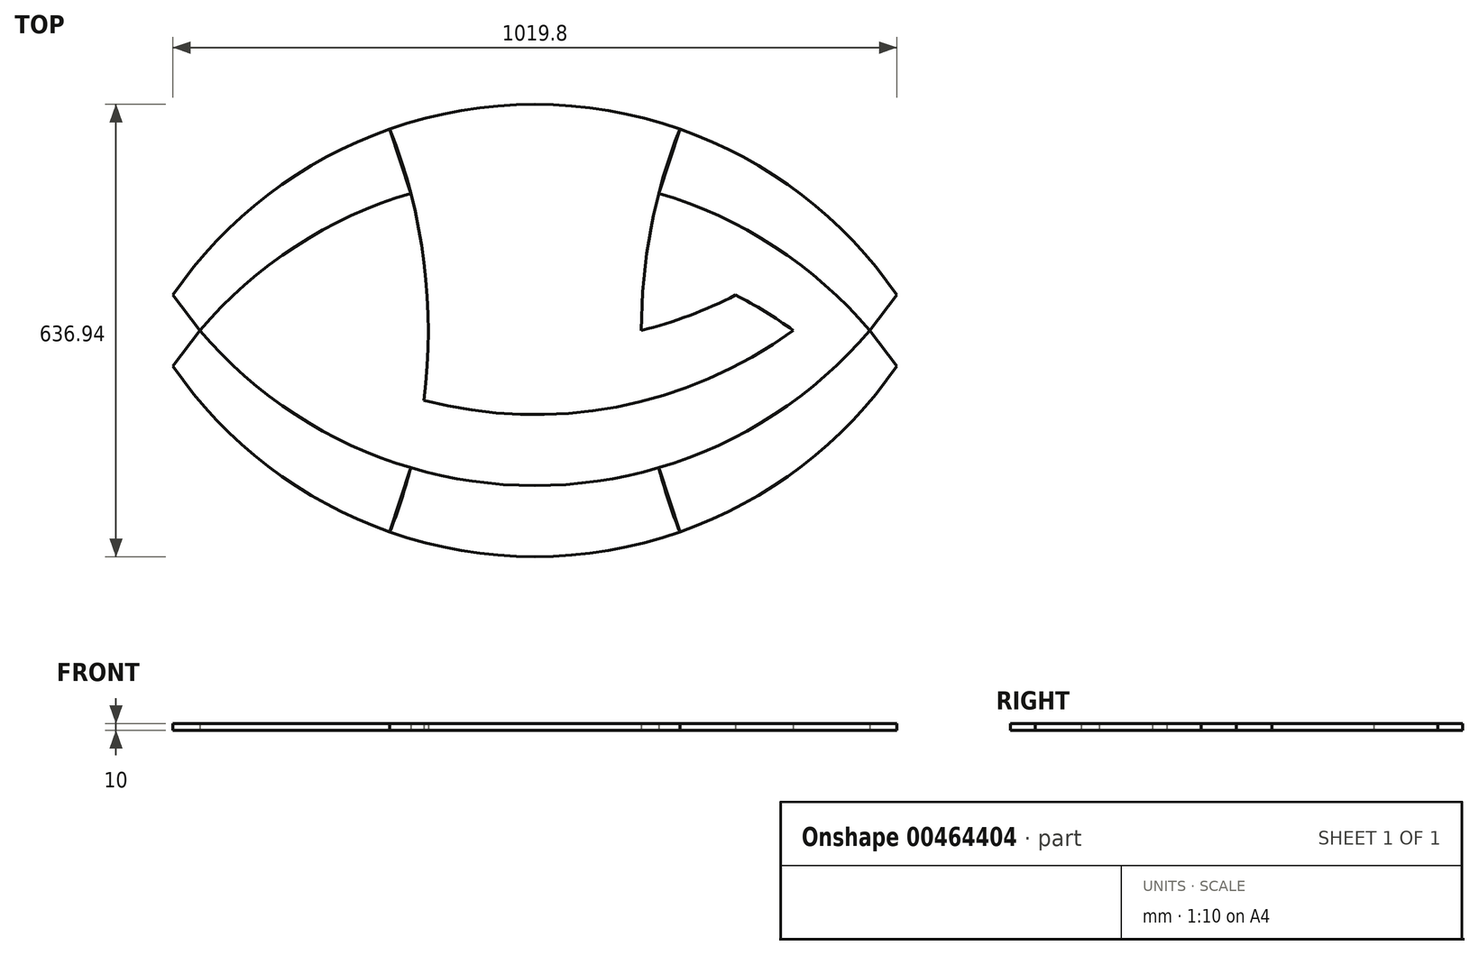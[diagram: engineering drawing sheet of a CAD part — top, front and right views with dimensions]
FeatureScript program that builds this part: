
annotation { "Feature Type Name" : "Feature", "Feature Type Description" : "" }
export const myFeature = defineFeature(function(context is Context, id is Id, definition is map)
    precondition{}
    {
        {
            var Q0;
            Q0=qCreatedBy(makeId("Top.planeOp"),FACE);
            var sketch = newSketch(context, id + "F0", { "sketchPlane" : qUnion([Q0])});
            skLineSegment(sketch, "E0", {"start": v(0, 652.5) * mm, "end": v(0, -479.98) * mm, "construction": true});
            skLineSegment(sketch, "E1", {"start": v(-841.35, 0) * mm, "end": v(906.92, 0) * mm, "construction": true});
            skLineSegment(sketch, "E2.bottom", {"start": v(150, 300) * mm, "end": v(-150, 300) * mm, "construction": true});
            skLineSegment(sketch, "E2.top", {"start": v(150, -300) * mm, "end": v(-150, -300) * mm, "construction": true});
            skLineSegment(sketch, "E2.left", {"start": v(150, 300) * mm, "end": v(150, -300) * mm, "construction": true});
            skLineSegment(sketch, "E2.right", {"start": v(-150, 300) * mm, "end": v(-150, -300) * mm, "construction": true});
            skPoint(sketch, "E2.middle", {"position": v(0, 0) * mm});
            skCircle(sketch, "E3", {"center": v(0, 0) * mm, "radius": 300 * mm, "construction": true});
            skCircle(sketch, "E4", {"center": v(0, -300) * mm, "radius": 618.47 * mm});
            skCircle(sketch, "E5", {"center": v(0, 0) * mm, "radius": 918.47 * mm, "construction": true});
            skCircle(sketch, "E6", {"center": v(918.47, 0) * mm, "radius": 768.47 * mm});
            skCircle(sketch, "E7", {"center": v(-918.47, 0) * mm, "radius": 768.47 * mm});
            skLineSegment(sketch, "E8", {"start": v(-839.1, -50) * mm, "end": v(1037.37, -50) * mm, "construction": true});
            skLineSegment(sketch, "E9.MirrorCS", {"start": v(-839.1, 50) * mm, "end": v(1037.37, 50) * mm, "construction": true});
            skCircle(sketch, "E10.MirrorC", {"center": v(0, 400) * mm, "radius": 618.47 * mm});
            skCircle(sketch, "E11.MirrorC", {"center": v(0, -200) * mm, "radius": 618.47 * mm});
            skCircle(sketch, "E12.MirrorC", {"center": v(0, -400) * mm, "radius": 618.47 * mm});
            skCircle(sketch, "E13.MirrorC", {"center": v(0, -500) * mm, "radius": 618.47 * mm});
            skCircle(sketch, "E14.MirrorC", {"center": v(0, 100) * mm, "radius": 618.47 * mm});
            skCircle(sketch, "E15.MirrorC", {"center": v(0, 200) * mm, "radius": 618.47 * mm});
            skCircle(sketch, "E16.MirrorC", {"center": v(0, 600) * mm, "radius": 618.47 * mm});
            skCircle(sketch, "E17.MirrorC", {"center": v(0, 500) * mm, "radius": 618.47 * mm});
            skCircle(sketch, "E18.MirrorC", {"center": v(0, 300) * mm, "radius": 618.47 * mm});
            skLineSegment(sketch, "E19", {"start": v(-509.9, 50) * mm, "end": v(-471.7, 0) * mm});
            skLineSegment(sketch, "E20", {"start": v(-471.7, 0) * mm, "end": v(-509.9, -50) * mm});
            skLineSegment(sketch, "E21", {"start": v(509.9, 50) * mm, "end": v(471.7, 0) * mm});
            skLineSegment(sketch, "E22", {"start": v(471.7, 0) * mm, "end": v(509.9, -50) * mm});
            skLineSegment(sketch, "E23", {"start": v(204.3, 283.75) * mm, "end": v(174.7, 193.28) * mm});
            skLineSegment(sketch, "E24", {"start": v(204.3, -283.75) * mm, "end": v(174.7, -193.28) * mm});
            skLineSegment(sketch, "E25", {"start": v(-204.3, -283.75) * mm, "end": v(-174.7, -193.28) * mm});
            skLineSegment(sketch, "E26", {"start": v(-204.3, 283.75) * mm, "end": v(-174.7, 193.28) * mm});
            skSolve(sketch);
        }
        {
            var Q0;
            {var subQ0=sQuery(id+"F0.wireOp",EDGE,"E17.MirrorC");var subQ1=sQuery(id+"F0.wireOp",EDGE,"E4");var subQ2=makeQuery(id+"F0.imprint","INTERSECT",VERTEX,{"disambiguationData":[OD(1.0)],"derivedFrom":[subQ1,subQ0]});Q0=makeQuery(id+"F0.imprint","IMPRINT",FACE,{"disambiguationData":[TD([[makeQuery(id+"F0.imprint","IMPRINT",EDGE,{"disambiguationData":[TD([[subQ2,-1.0]])],"derivedFrom":subQ1}),1.0]])]});}
            var Q1;
            {var subQ0=sQuery(id+"F0.wireOp",EDGE,"E16.MirrorC");var subQ1=sQuery(id+"F0.wireOp",EDGE,"E4");var subQ2=makeQuery(id+"F0.imprint","INTERSECT",VERTEX,{"disambiguationData":[OD(1.0)],"derivedFrom":[subQ1,subQ0]});Q1=makeQuery(id+"F0.imprint","IMPRINT",FACE,{"disambiguationData":[TD([[makeQuery(id+"F0.imprint","IMPRINT",EDGE,{"disambiguationData":[TD([[subQ2,-1.0]])],"derivedFrom":subQ1}),1.0]])]});}
            var Q2;
            {var subQ0=sQuery(id+"F0.wireOp",EDGE,"7089ef92-c8cd-43ee-9cd9-a57d0f0e25173.MirrorC");var subQ1=sQuery(id+"F0.wireOp",EDGE,"E12.MirrorC");var subQ2=makeQuery(id+"F0.imprint","INTERSECT",VERTEX,{"disambiguationData":[OD(1.0)],"derivedFrom":[subQ1,subQ0]});Q2=makeQuery(id+"F0.imprint","IMPRINT",FACE,{"disambiguationData":[TD([[makeQuery(id+"F0.imprint","IMPRINT",EDGE,{"disambiguationData":[TD([[subQ2,-1.0]])],"derivedFrom":subQ1}),1.0]])]});}
            var Q3;
            {var subQ0=sQuery(id+"F0.wireOp",EDGE,"7089ef92-c8cd-43ee-9cd9-a57d0f0e25173.MirrorC");var subQ1=sQuery(id+"F0.wireOp",EDGE,"E6");var subQ2=makeQuery(id+"F0.imprint","INTERSECT",VERTEX,{"disambiguationData":[OD(1.0)],"derivedFrom":[subQ1,subQ0]});Q3=makeQuery(id+"F0.imprint","IMPRINT",FACE,{"disambiguationData":[TD([[makeQuery(id+"F0.imprint","IMPRINT",EDGE,{"disambiguationData":[TD([[subQ2,-1.0]])],"derivedFrom":subQ1}),1.0]])]});}
            var Q4;
            {var subQ0=sQuery(id+"F0.wireOp",EDGE,"7089ef92-c8cd-43ee-9cd9-a57d0f0e25173.MirrorC");var subQ1=sQuery(id+"F0.wireOp",EDGE,"E4");var subQ2=makeQuery(id+"F0.imprint","INTERSECT",VERTEX,{"disambiguationData":[OD(0.0)],"derivedFrom":[subQ1,subQ0]});Q4=makeQuery(id+"F0.imprint","IMPRINT",FACE,{"disambiguationData":[TD([[makeQuery(id+"F0.imprint","IMPRINT",EDGE,{"disambiguationData":[TD([[subQ2,-1.0]])],"derivedFrom":subQ1}),1.0]])]});}
            var Q5;
            {var subQ0=sQuery(id+"F0.wireOp",EDGE,"E17.MirrorC");var subQ1=sQuery(id+"F0.wireOp",EDGE,"E4");var subQ2=makeQuery(id+"F0.imprint","INTERSECT",VERTEX,{"disambiguationData":[OD(0.0)],"derivedFrom":[subQ1,subQ0]});Q5=makeQuery(id+"F0.imprint","IMPRINT",FACE,{"disambiguationData":[TD([[makeQuery(id+"F0.imprint","IMPRINT",EDGE,{"disambiguationData":[TD([[subQ2,-1.0]])],"derivedFrom":subQ1}),1.0]])]});}
            var Q6;
            {var subQ0=sQuery(id+"F0.wireOp",EDGE,"E20");Q6=makeQuery(id+"F0.imprint","IMPRINT",FACE,{"disambiguationData":[TD([[makeQuery(id+"F0.imprint","IMPRINT",EDGE,{"derivedFrom":subQ0}),1.0]])]});}
            var Q7;
            {var subQ0=sQuery(id+"F0.wireOp",EDGE,"E22");Q7=makeQuery(id+"F0.imprint","IMPRINT",FACE,{"disambiguationData":[TD([[makeQuery(id+"F0.imprint","IMPRINT",EDGE,{"derivedFrom":subQ0}),-1.0]])]});}
            var Q8;
            {var subQ0=sQuery(id+"F0.wireOp",EDGE,"E21");Q8=makeQuery(id+"F0.imprint","IMPRINT",FACE,{"disambiguationData":[TD([[makeQuery(id+"F0.imprint","IMPRINT",EDGE,{"derivedFrom":subQ0}),-1.0]])]});}
            var Q9;
            {var subQ0=sQuery(id+"F0.wireOp",EDGE,"E26");Q9=makeQuery(id+"F0.imprint","IMPRINT",FACE,{"disambiguationData":[TD([[makeQuery(id+"F0.imprint","IMPRINT",EDGE,{"derivedFrom":subQ0}),-1.0]])]});}
            var Q10;
            {var subQ0=sQuery(id+"F0.wireOp",EDGE,"E25");Q10=makeQuery(id+"F0.imprint","IMPRINT",FACE,{"disambiguationData":[TD([[makeQuery(id+"F0.imprint","IMPRINT",EDGE,{"derivedFrom":subQ0}),1.0]])]});}
            var Q11;
            {var subQ0=sQuery(id+"F0.wireOp",EDGE,"E24");Q11=makeQuery(id+"F0.imprint","IMPRINT",FACE,{"disambiguationData":[TD([[makeQuery(id+"F0.imprint","IMPRINT",EDGE,{"derivedFrom":subQ0}),-1.0]])]});}
            var Q12;
            {var subQ0=sQuery(id+"F0.wireOp",EDGE,"E23");Q12=makeQuery(id+"F0.imprint","IMPRINT",FACE,{"disambiguationData":[TD([[makeQuery(id+"F0.imprint","IMPRINT",EDGE,{"derivedFrom":subQ0}),1.0]])]});}
            extrude(context, id + "F1", {"entities" : qUnion([Q0, Q1, Q2, Q3, Q4, Q5, Q6, Q7, Q8, Q9, Q10, Q11, Q12]), "depth" : 10 * mm});
        }
        {
            var Q0;
            {var subQ0=sQuery(id+"F0.wireOp",EDGE,"E23");var subQ1=sQuery(id+"F0.wireOp",EDGE,"E6");var subQ2=sQuery(id+"F0.wireOp",EDGE,"E4");var subQ3=makeQuery(id+"F0.imprint","INTERSECT",VERTEX,{"derivedFrom":[subQ2,subQ1,subQ0]});Q0=makeQuery(id+"F0.imprint","IMPRINT",FACE,{"disambiguationData":[TD([[makeQuery(id+"F0.imprint","IMPRINT",EDGE,{"disambiguationData":[TD([[subQ3,-1.0]])],"derivedFrom":subQ2}),1.0]])]});}
            var Q1;
            {var subQ1=sQuery(id+"F0.wireOp",EDGE,"E6");var subQ3=sQuery(id+"F0.wireOp",EDGE,"E13.MirrorC");var subQ4=makeQuery(id+"F0.imprint","INTERSECT",VERTEX,{"disambiguationData":[OD(1.0)],"derivedFrom":[subQ1,subQ3]});Q1=makeQuery(id+"F0.imprint","IMPRINT",FACE,{"disambiguationData":[TD([[makeQuery(id+"F0.imprint","IMPRINT",EDGE,{"disambiguationData":[TD([[subQ4,-1.0]])],"derivedFrom":subQ3}),-1.0]])]});}
            var Q2;
            {var subQ0=sQuery(id+"F0.wireOp",EDGE,"E13.MirrorC");var subQ1=sQuery(id+"F0.wireOp",EDGE,"E6");var subQ2=makeQuery(id+"F0.imprint","INTERSECT",VERTEX,{"disambiguationData":[OD(1.0)],"derivedFrom":[subQ1,subQ0]});Q2=makeQuery(id+"F0.imprint","IMPRINT",FACE,{"disambiguationData":[TD([[makeQuery(id+"F0.imprint","IMPRINT",EDGE,{"disambiguationData":[TD([[subQ2,-1.0]])],"derivedFrom":subQ1}),-1.0]])]});}
            var Q3;
            {var subQ0=sQuery(id+"F0.wireOp",EDGE,"E16.MirrorC");var subQ1=sQuery(id+"F0.wireOp",EDGE,"E6");var subQ2=makeQuery(id+"F0.imprint","INTERSECT",VERTEX,{"disambiguationData":[OD(1.0)],"derivedFrom":[subQ1,subQ0]});Q3=makeQuery(id+"F0.imprint","IMPRINT",FACE,{"disambiguationData":[TD([[makeQuery(id+"F0.imprint","IMPRINT",EDGE,{"disambiguationData":[TD([[subQ2,-1.0]])],"derivedFrom":subQ1}),-1.0]])]});}
            var Q4;
            {var subQ1=sQuery(id+"F0.wireOp",EDGE,"E6");var subQ3=sQuery(id+"F0.wireOp",EDGE,"E17.MirrorC");var subQ4=makeQuery(id+"F0.imprint","INTERSECT",VERTEX,{"disambiguationData":[OD(1.0)],"derivedFrom":[subQ1,subQ3]});Q4=makeQuery(id+"F0.imprint","IMPRINT",FACE,{"disambiguationData":[TD([[makeQuery(id+"F0.imprint","IMPRINT",EDGE,{"disambiguationData":[TD([[subQ4,-1.0]])],"derivedFrom":subQ3}),1.0]])]});}
            var Q5;
            {var subQ0=sQuery(id+"F0.wireOp",EDGE,"E24");var subQ1=sQuery(id+"F0.wireOp",EDGE,"E18.MirrorC");var subQ2=sQuery(id+"F0.wireOp",EDGE,"E6");var subQ3=makeQuery(id+"F0.imprint","INTERSECT",VERTEX,{"derivedFrom":[subQ2,subQ1,subQ0]});Q5=makeQuery(id+"F0.imprint","IMPRINT",FACE,{"disambiguationData":[TD([[makeQuery(id+"F0.imprint","IMPRINT",EDGE,{"disambiguationData":[TD([[subQ3,1.0]])],"derivedFrom":subQ2}),-1.0]])]});}
            extrude(context, id + "F2", {"entities" : qUnion([Q0, Q1, Q2, Q3, Q4, Q5]), "depth" : 10 * mm});
        }
    });
